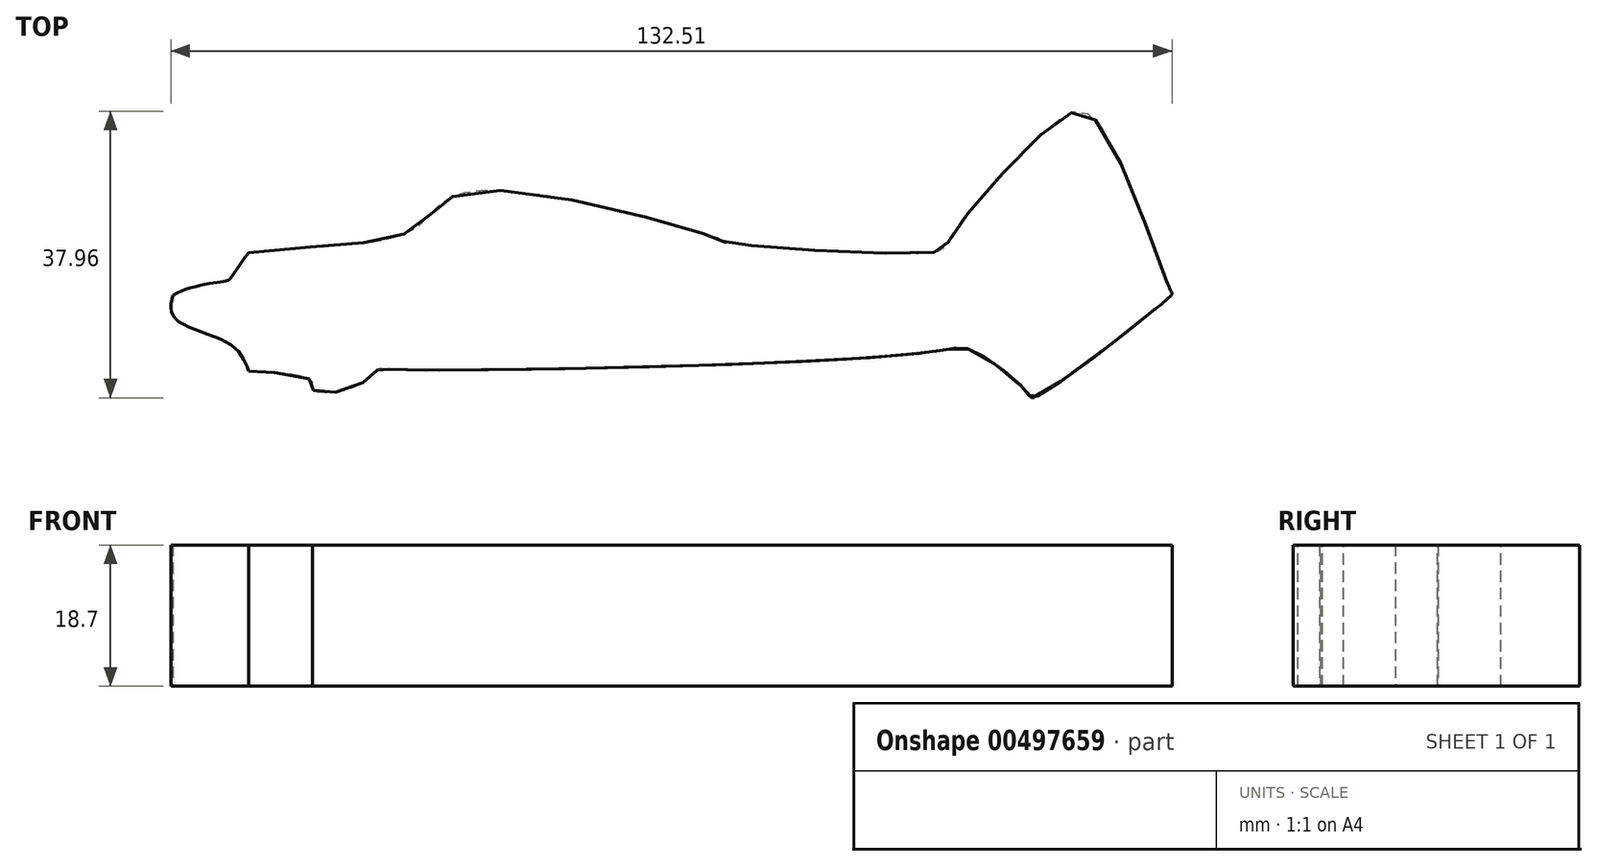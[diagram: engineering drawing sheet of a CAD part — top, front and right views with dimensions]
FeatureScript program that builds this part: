
annotation { "Feature Type Name" : "Feature", "Feature Type Description" : "" }
export const myFeature = defineFeature(function(context is Context, id is Id, definition is map)
    precondition{}
    {
        {
            var Q0;
            Q0=qCreatedBy(makeId("Top.planeOp"),FACE);
            var sketch = newSketch(context, id + "F0", { "sketchPlane" : qUnion([Q0])});
            skFitSpline(sketch, "E0", {"points": [v(-59.06, 5.66) * mm, v(-37.27, 8.76) * mm, v(-29.96, 13.76) * mm, v(3.03, 7.5) * mm, v(4.28, 7.02) * mm, v(31.8, 5.77) * mm, v(33.81, 7.6) * mm, v(47.57, 22.8) * mm, v(53.24, 23) * mm, v(63, 0.63) * mm, v(63.02, 0) * mm, v(44.94, -13.49) * mm, v(43.97, -12.84) * mm, v(36.63, -7.22) * mm, v(32.96, -7.22) * mm, v(0, -9.26) * mm, v(-40.84, -9.73) * mm, v(-41.93, -9.79) * mm, v(-44.9, -12.08) * mm, v(-50.5, -12.48) * mm, v(-50.85, -11.16) * mm, v(-59.03, -10.02) * mm, v(-59.04, -10.01) * mm], "startDerivative": vector(405.42, 51.23) * mm, "endDerivative": vector(-0.37, 3.23) * mm});
            skFitSpline(sketch, "E1", {"points": [v(-69.08, 0) * mm, v(-68.73, -3.08) * mm, v(-61.52, -6.47) * mm, v(-59.03, -10.02) * mm], "startDerivative": vector(-3.44, -13.38) * mm, "endDerivative": vector(4.75, -12.55) * mm});
            skFitSpline(sketch, "E2", {"points": [v(-59.06, 5.66) * mm, v(-62.24, 1.9) * mm, v(-69.08, 0) * mm], "startDerivative": vector(-17.09, -22.71) * mm, "endDerivative": vector(-12.15, -7.52) * mm});
            skPoint(sketch, "E3", {"position": v(-60.93, 3) * mm});
            skLineSegment(sketch, "E4", {"start": v(62.18, 2.62) * mm, "end": v(42.1, 2.62) * mm});
            skLineSegment(sketch, "E5", {"start": v(42.1, 2.62) * mm, "end": v(27.1, 2.62) * mm});
            skLineSegment(sketch, "E6", {"start": v(27.1, 2.62) * mm, "end": v(27.18, -1.79) * mm});
            skLineSegment(sketch, "E7", {"start": v(27.18, -1.79) * mm, "end": v(61.09, -1.72) * mm});
            skFitSpline(sketch, "E8.trimOffspring", {"points": [v(-59.06, 5.66) * mm, v(-37.27, 8.76) * mm, v(-29.96, 13.76) * mm, v(3.03, 7.5) * mm, v(4.28, 7.02) * mm, v(31.8, 5.77) * mm, v(33.81, 7.6) * mm, v(47.57, 22.8) * mm, v(53.24, 23) * mm, v(63, 0.63) * mm, v(63.02, 0) * mm, v(44.94, -13.49) * mm, v(43.97, -12.84) * mm, v(36.63, -7.22) * mm, v(32.96, -7.22) * mm, v(0, -9.26) * mm, v(-40.84, -9.73) * mm, v(-41.93, -9.79) * mm, v(-44.9, -12.08) * mm, v(-50.5, -12.48) * mm, v(-50.85, -11.16) * mm, v(-59.03, -10.02) * mm, v(-59.04, -10.01) * mm], "startDerivative": vector(405.42, 51.23) * mm, "endDerivative": vector(-0.37, 3.23) * mm});
            skSolve(sketch);
        }
        {
            var Q0;
            Q0 = qSketchRegion(id + "F0", true);
            extrude(context, id + "F1", {"entities" : qUnion([Q0]), "depth" : 18.7 * mm});
        }
    });
